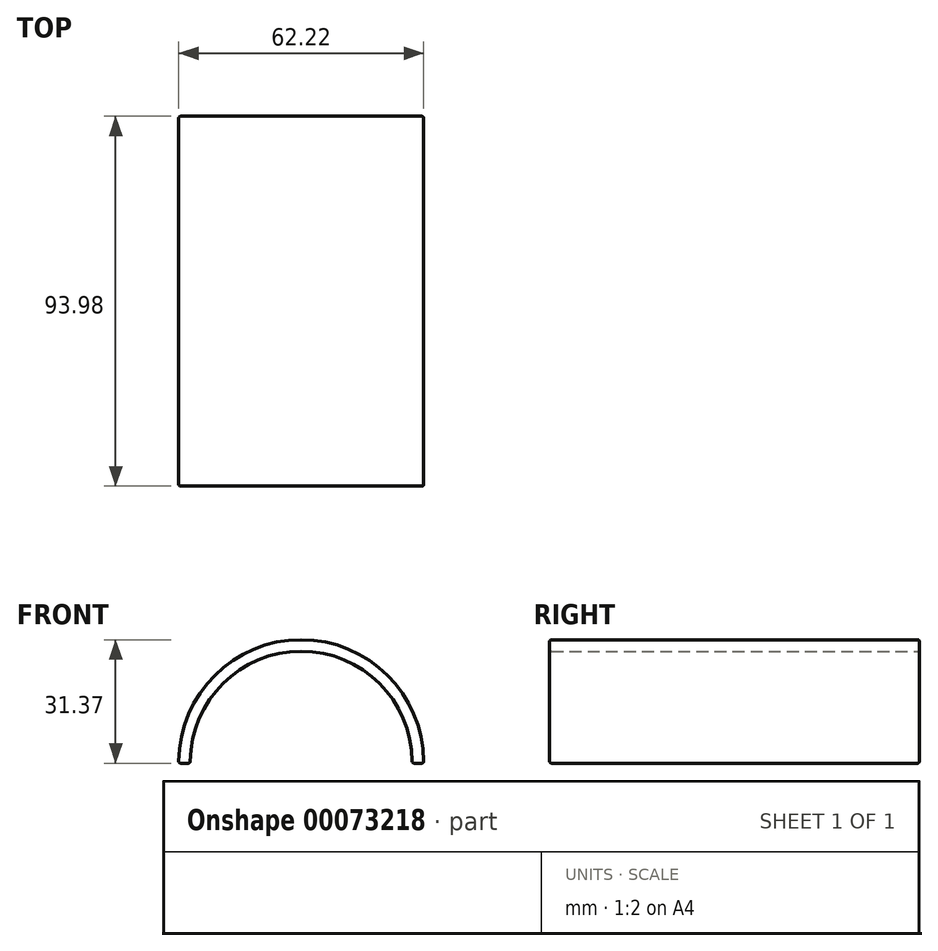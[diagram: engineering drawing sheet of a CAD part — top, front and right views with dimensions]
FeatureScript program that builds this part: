
annotation { "Feature Type Name" : "Feature", "Feature Type Description" : "" }
export const myFeature = defineFeature(function(context is Context, id is Id, definition is map)
    precondition{}
    {
        {
            var Q0;
            Q0=qCreatedBy(makeId("Front.planeOp"),FACE);
            var sketch = newSketch(context, id + "F0", { "sketchPlane" : qUnion([Q0])});
            skArc(sketch, "E0", {"start": v(31.11, 0) * mm, "mid": v(0, 31.37) * mm, "end": v(-31.11, 0) * mm});
            skArc(sketch, "E1", {"start": v(28.2, 0) * mm, "mid": v(0, 28.45) * mm, "end": v(-28.2, 0) * mm});
            skLineSegment(sketch, "E2", {"start": v(-31.11, 0) * mm, "end": v(-28.2, 0) * mm});
            skLineSegment(sketch, "E3.MirrorCS", {"start": v(31.11, 0) * mm, "end": v(28.2, 0) * mm});
            skSolve(sketch);
        }
        {
            var Q0;
            Q0=makeQuery(id+"F0.imprint","IMPRINT",FACE,{"disambiguationData":[TD([[makeQuery(id+"F0.imprint","IMPRINT",EDGE,{"derivedFrom":sQuery(id+"F0.wireOp",EDGE,"E0")}),1.0]])]});
            extrude(context, id + "F1", {"entities" : qUnion([Q0]), "depth" : 93.98 * mm});
        }
        {
            var Q0;
            Q0=makeQuery(id+"F1.opExtrude","CAP_EDGE",EDGE,{"disambiguationData":[OSD([sQuery(id+"F0.wireOp",EDGE,"E1")])],"isStart":false});
            var Q1;
            Q1=makeQuery(id+"F1.opExtrude","CAP_EDGE",EDGE,{"disambiguationData":[OSD([sQuery(id+"F0.wireOp",EDGE,"E0")])],"isStart":false});
            var Q2;
            Q2=makeQuery(id+"F1.opExtrude","SWEPT_EDGE",EDGE,{"disambiguationData":[OSD([sQuery(id+"F0.wireOp",EDGE,"E0"),sQuery(id+"F0.wireOp",EDGE,"E3.MirrorCS")])]});
            var Q3;
            Q3=makeQuery(id+"F1.opExtrude","SWEPT_EDGE",EDGE,{"disambiguationData":[OSD([sQuery(id+"F0.wireOp",EDGE,"E1"),sQuery(id+"F0.wireOp",EDGE,"E3.MirrorCS")])]});
            var Q4;
            Q4=makeQuery(id+"F1.opExtrude","SWEPT_EDGE",EDGE,{"disambiguationData":[OSD([sQuery(id+"F0.wireOp",EDGE,"E1"),sQuery(id+"F0.wireOp",EDGE,"E2")])]});
            var Q5;
            Q5=makeQuery(id+"F1.opExtrude","SWEPT_EDGE",EDGE,{"disambiguationData":[OSD([sQuery(id+"F0.wireOp",EDGE,"E0"),sQuery(id+"F0.wireOp",EDGE,"E2")])]});
            var Q6;
            Q6=makeQuery(id+"F1.opExtrude","CAP_EDGE",EDGE,{"disambiguationData":[OSD([sQuery(id+"F0.wireOp",EDGE,"E2")])],"isStart":false});
            var Q7;
            Q7=makeQuery(id+"F1.opExtrude","CAP_EDGE",EDGE,{"disambiguationData":[OSD([sQuery(id+"F0.wireOp",EDGE,"E2")])],"isStart":true});
            var Q8;
            Q8=makeQuery(id+"F1.opExtrude","CAP_EDGE",EDGE,{"disambiguationData":[OSD([sQuery(id+"F0.wireOp",EDGE,"E3.MirrorCS")])],"isStart":true});
            var Q9;
            Q9=makeQuery(id+"F1.opExtrude","CAP_EDGE",EDGE,{"disambiguationData":[OSD([sQuery(id+"F0.wireOp",EDGE,"E0")])],"isStart":true});
            var Q10;
            Q10=makeQuery(id+"F1.opExtrude","CAP_EDGE",EDGE,{"disambiguationData":[OSD([sQuery(id+"F0.wireOp",EDGE,"E1")])],"isStart":true});
            var Q11;
            Q11=makeQuery(id+"F1.opExtrude","CAP_EDGE",EDGE,{"disambiguationData":[OSD([sQuery(id+"F0.wireOp",EDGE,"E3.MirrorCS")])],"isStart":false});
            fillet(context, id + "F2", {"entities" : qUnion([Q0, Q1, Q2, Q3, Q4, Q5, Q6, Q7, Q8, Q9, Q10, Q11]), "radius" : 0.5 * mm, "tangentPropagation" : true, "allowEdgeOverflow" : false});
        }
    });
